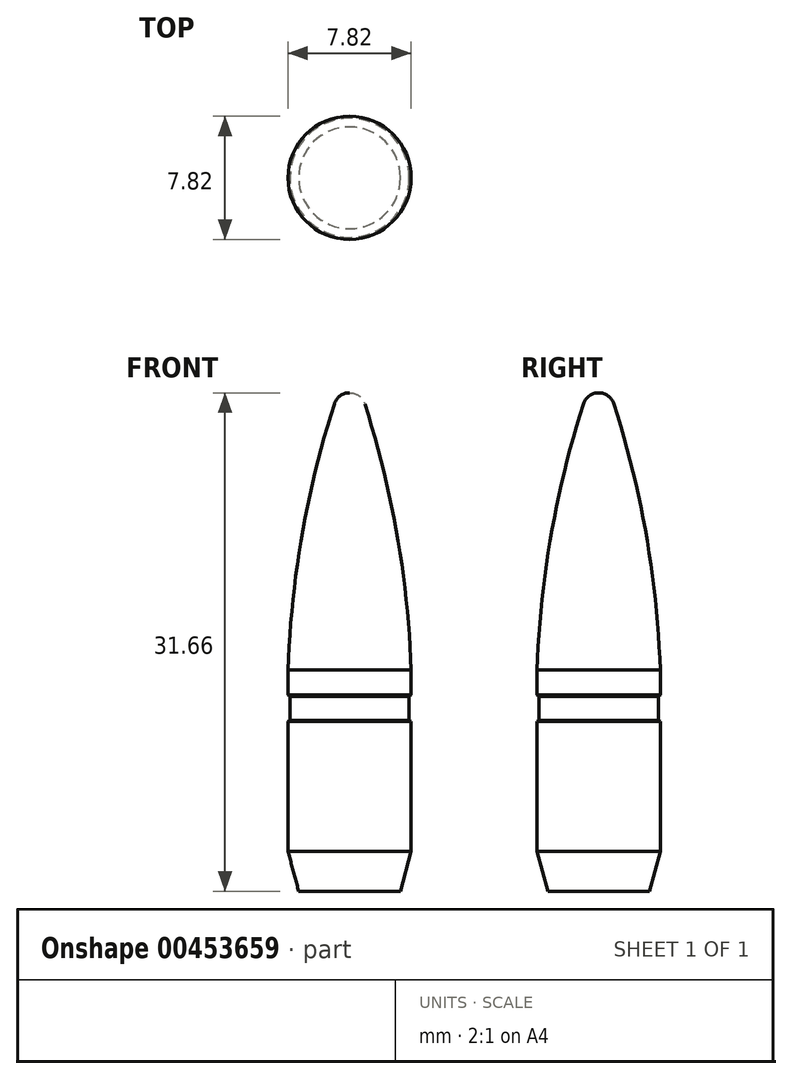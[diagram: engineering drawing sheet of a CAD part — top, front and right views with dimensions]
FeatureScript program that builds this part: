
annotation { "Feature Type Name" : "Feature", "Feature Type Description" : "" }
export const myFeature = defineFeature(function(context is Context, id is Id, definition is map)
    precondition{}
    {
        {
            var Q0;
            Q0=qCreatedBy(makeId("Front.planeOp"),FACE);
            var sketch = newSketch(context, id + "F0", { "sketchPlane" : qUnion([Q0])});
            skLineSegment(sketch, "E0", {"start": v(3.91, 14.05) * mm, "end": v(3.91, 12.47) * mm});
            skLineSegment(sketch, "E1", {"start": v(3.91, 12.47) * mm, "end": v(3.78, 12.4) * mm});
            skLineSegment(sketch, "E2", {"start": v(3.78, 12.4) * mm, "end": v(3.78, 10.87) * mm});
            skLineSegment(sketch, "E3", {"start": v(3.78, 10.87) * mm, "end": v(3.91, 10.8) * mm});
            skLineSegment(sketch, "E4", {"start": v(3.91, 10.8) * mm, "end": v(3.91, 2.54) * mm});
            skLineSegment(sketch, "E5", {"start": v(3.91, 2.54) * mm, "end": v(3.23, 0) * mm});
            skLineSegment(sketch, "E6", {"start": v(3.23, 0) * mm, "end": v(0, 0) * mm});
            skLineSegment(sketch, "E7", {"start": v(0, 0) * mm, "end": v(0, 31.66) * mm});
            skArc(sketch, "E8", {"start": v(0, 31.66) * mm, "mid": v(0.6, 31.47) * mm, "end": v(0.97, 30.96) * mm});
            skArc(sketch, "E9.trimOffspring", {"start": v(0.97, 30.96) * mm, "mid": v(3.02, 22.6) * mm, "end": v(3.91, 14.05) * mm});
            skLineSegment(sketch, "E10", {"start": v(-58.64, 11.87) * mm, "end": v(3.91, 14.05) * mm, "construction": true});
            skSolve(sketch);
        }
        {
            var Q0;
            Q0 = qSketchRegion(id + "F0", true);
            var Q1;
            Q1=sQuery(id+"F0.wireOp",EDGE,"E7");
            revolve(context, id + "F1", {"entities" : qUnion([Q0]), "axis" : qUnion([Q1]), "revolveType" : RevolveType.FULL});
        }
    });
